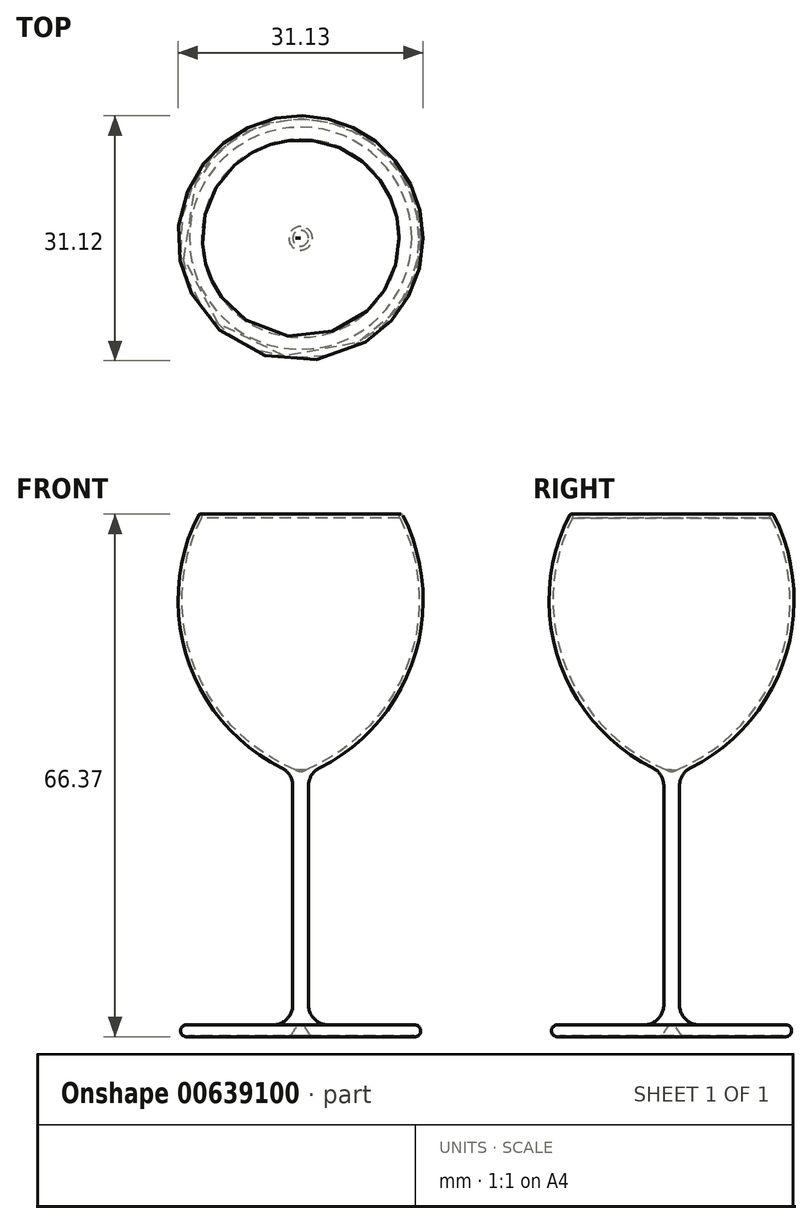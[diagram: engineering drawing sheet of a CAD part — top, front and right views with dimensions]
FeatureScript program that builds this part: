
annotation { "Feature Type Name" : "Feature", "Feature Type Description" : "" }
export const myFeature = defineFeature(function(context is Context, id is Id, definition is map)
    precondition{}
    {
        {
            var Q0;
            Q0=qCreatedBy(makeId("Front.planeOp"),FACE);
            var sketch = newSketch(context, id + "F0", { "sketchPlane" : qUnion([Q0])});
            skArc(sketch, "E0", {"start": v(-11.94, 32) * mm, "mid": v(-12.93, 13.4) * mm, "end": v(0, 0) * mm});
            skArc(sketch, "E1.0", {"start": v(-12.33, 32.32) * mm, "mid": v(-13.7, 14.08) * mm, "end": v(-1.74, 0.25) * mm});
            skLineSegment(sketch, "E2", {"start": v(-0.34, -2.03) * mm, "end": v(-0.34, -29.86) * mm});
            skLineSegment(sketch, "E3", {"start": v(-2.88, -32.4) * mm, "end": v(-13.84, -32.4) * mm});
            skPoint(sketch, "E4.visualSharp", {"position": v(-0.34, -32.4) * mm});
            skArc(sketch, "E4.filletArc", {"start": v(-2.88, -32.4) * mm, "mid": v(-1.08, -31.66) * mm, "end": v(-0.34, -29.86) * mm});
            skLineSegment(sketch, "E5", {"start": v(-13.84, -33.8) * mm, "end": v(-0.84, -33.8) * mm});
            skArc(sketch, "E6", {"start": v(-13.84, -32.4) * mm, "mid": v(-14.56, -33.35) * mm, "end": v(-13.46, -33.8) * mm});
            skFitSpline(sketch, "E7", {"points": [v(0, 0) * mm, v(0.66, -0.25) * mm], "startDerivative": vector(1.1, -0.46) * mm, "endDerivative": vector(1.81, -0.57) * mm});
            skFitSpline(sketch, "E8", {"points": [v(-0.84, -33.8) * mm, v(0.66, -32.4) * mm], "startDerivative": vector(1.88, 0.43) * mm, "endDerivative": vector(2.45, 0.5) * mm});
            skLineSegment(sketch, "E9", {"start": v(0.66, -0.25) * mm, "end": v(0.66, -32.4) * mm});
            skArc(sketch, "E10", {"start": v(-12.33, 32.32) * mm, "mid": v(-11.93, 32.4) * mm, "end": v(-11.94, 32) * mm});
            skPoint(sketch, "E11.visualSharp", {"position": v(-0.34, -0.4) * mm});
            skArc(sketch, "E11.filletArc", {"start": v(-0.34, -2.03) * mm, "mid": v(-0.72, -0.7) * mm, "end": v(-1.74, 0.25) * mm});
            skSolve(sketch);
        }
        {
            var Q0;
            Q0 = qSketchRegion(id + "F0", true);
            var Q1;
            Q1 = qConstructionFilter(qBodyType(qCreatedBy(id + "F0" ,EDGE), BodyType.WIRE), ConstructionObject.NO);
            var Q2;
            Q2=sQuery(id+"F0.wireOp",EDGE,"E9");
            revolve(context, id + "F1", {"entities" : qUnion([Q0]), "surfaceEntities" : qUnion([Q1]), "axis" : qUnion([Q2]), "revolveType" : RevolveType.FULL});
        }
    });
